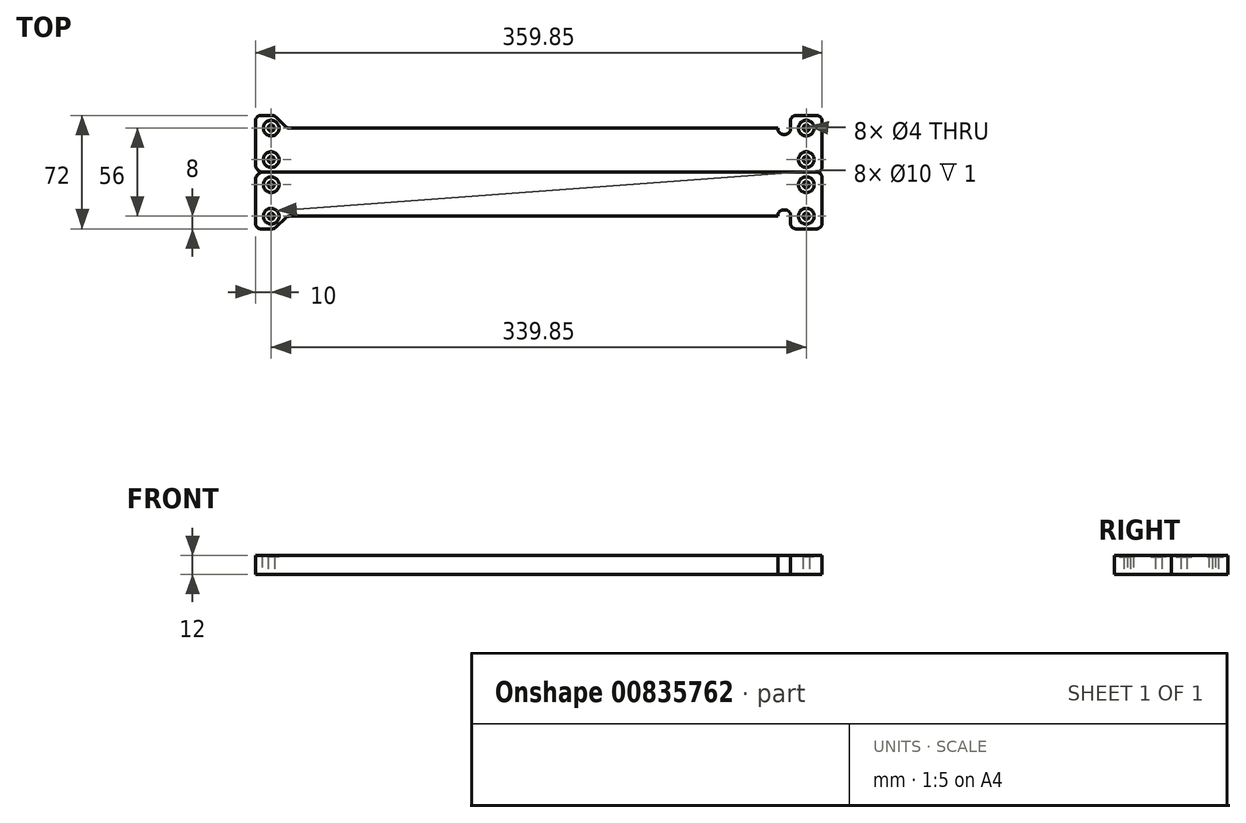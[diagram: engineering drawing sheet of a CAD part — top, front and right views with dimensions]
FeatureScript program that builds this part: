
annotation { "Feature Type Name" : "Feature", "Feature Type Description" : "" }
export const myFeature = defineFeature(function(context is Context, id is Id, definition is map)
    precondition{}
    {
        {
            var Q0;
            Q0=qCreatedBy(makeId("Top.planeOp"),FACE);
            var sketch = newSketch(context, id + "F0", { "sketchPlane" : qUnion([Q0])});
            skLineSegment(sketch, "E0", {"start": v(0, 0) * mm, "end": v(0, 28) * mm, "construction": true});
            skLineSegment(sketch, "E1", {"start": v(1.4, 28) * mm, "end": v(311.85, 28) * mm});
            skLineSegment(sketch, "E2", {"start": v(319.85, 28) * mm, "end": v(319.85, 32.6) * mm});
            skLineSegment(sketch, "E3", {"start": v(323.25, 36) * mm, "end": v(336.45, 36) * mm});
            skLineSegment(sketch, "E4", {"start": v(339.85, 32.6) * mm, "end": v(339.85, 3.4) * mm});
            skLineSegment(sketch, "E5", {"start": v(336.45, 0) * mm, "end": v(329.85, 0) * mm});
            skLineSegment(sketch, "E6", {"start": v(-1, 29) * mm, "end": v(-7, 35) * mm});
            skLineSegment(sketch, "E7", {"start": v(-9.4, 36) * mm, "end": v(-16.6, 36) * mm});
            skLineSegment(sketch, "E8", {"start": v(-20, 32.6) * mm, "end": v(-20, 4.95) * mm});
            skLineSegment(sketch, "E9", {"start": v(-10, 36) * mm, "end": v(-10, 0) * mm, "construction": true});
            skCircle(sketch, "E10", {"center": v(-10, 28) * mm, "radius": 2 * mm});
            skCircle(sketch, "E11", {"center": v(-10, 8) * mm, "radius": 2 * mm});
            skCircle(sketch, "E12", {"center": v(-10, 28) * mm, "radius": 5 * mm});
            skCircle(sketch, "E13", {"center": v(-10, 8) * mm, "radius": 5 * mm});
            skLineSegment(sketch, "E14", {"start": v(329.85, 36) * mm, "end": v(329.85, 0) * mm, "construction": true});
            skCircle(sketch, "E15", {"center": v(329.85, 8) * mm, "radius": 2 * mm});
            skCircle(sketch, "E16", {"center": v(329.85, 28) * mm, "radius": 2 * mm});
            skCircle(sketch, "E17", {"center": v(329.85, 28) * mm, "radius": 5 * mm});
            skCircle(sketch, "E18", {"center": v(329.85, 8) * mm, "radius": 5 * mm});
            skLineSegment(sketch, "E19", {"start": v(319.85, 28) * mm, "end": v(319.85, 27.4) * mm});
            skLineSegment(sketch, "E20", {"start": v(316.45, 24) * mm, "end": v(315.25, 24) * mm});
            skLineSegment(sketch, "E21", {"start": v(311.85, 27.4) * mm, "end": v(311.85, 28) * mm});
            skPoint(sketch, "E22.visualSharp", {"position": v(319.85, 36) * mm});
            skArc(sketch, "E22.filletArc", {"start": v(323.25, 36) * mm, "mid": v(320.85, 35) * mm, "end": v(319.85, 32.6) * mm});
            skPoint(sketch, "E23.visualSharp", {"position": v(319.85, 24) * mm});
            skArc(sketch, "E23.filletArc", {"start": v(316.45, 24) * mm, "mid": v(318.85, 25) * mm, "end": v(319.85, 27.4) * mm});
            skPoint(sketch, "E24.visualSharp", {"position": v(311.85, 24) * mm});
            skArc(sketch, "E24.filletArc", {"start": v(311.85, 27.4) * mm, "mid": v(312.85, 25) * mm, "end": v(315.25, 24) * mm});
            skPoint(sketch, "E25.visualSharp", {"position": v(339.85, 36) * mm});
            skArc(sketch, "E25.filletArc", {"start": v(339.85, 32.6) * mm, "mid": v(338.85, 35) * mm, "end": v(336.45, 36) * mm});
            skPoint(sketch, "E26.visualSharp", {"position": v(339.85, 0) * mm});
            skArc(sketch, "E26.filletArc", {"start": v(336.45, 0) * mm, "mid": v(338.85, 1) * mm, "end": v(339.85, 3.4) * mm});
            skPoint(sketch, "E27.visualSharp", {"position": v(-8, 36) * mm});
            skArc(sketch, "E27.filletArc", {"start": v(-7, 35) * mm, "mid": v(-8.1, 35.74) * mm, "end": v(-9.4, 36) * mm});
            skPoint(sketch, "E28.visualSharp", {"position": v(-20, 36) * mm});
            skArc(sketch, "E28.filletArc", {"start": v(-16.6, 36) * mm, "mid": v(-19, 35) * mm, "end": v(-20, 32.6) * mm});
            skPoint(sketch, "E29.visualSharp", {"position": v(-20, 0) * mm});
            skPoint(sketch, "E30.visualSharp", {"position": v(0, 28) * mm});
            skArc(sketch, "E30.filletArc", {"start": v(-1, 29) * mm, "mid": v(0.1, 28.26) * mm, "end": v(1.4, 28) * mm});
            skLineSegment(sketch, "E31", {"start": v(329.85, 0) * mm, "end": v(0, 0) * mm});
            skArc(sketch, "E32.filletArc", {"start": v(-20, 4.95) * mm, "mid": v(-18.78, 1.68) * mm, "end": v(-15.73, 0) * mm});
            skLineSegment(sketch, "E33", {"start": v(0, -16.1) * mm, "end": v(215.82, -16.1) * mm, "construction": true});
            skLineSegment(sketch, "E34", {"start": v(-15.73, 0) * mm, "end": v(0, 0) * mm});
            skSolve(sketch);
        }
        {
            var Q0;
            Q0=qSketchRegion(id+"F0",true);
            var Q1;
            Q1=makeQuery(id+"F0.imprint","IMPRINT",FACE,{"disambiguationData":[TD([[makeQuery(id+"F0.imprint","IMPRINT",EDGE,{"derivedFrom":sQuery(id+"F0.wireOp",EDGE,"E10")}),-1.0]])]});
            var Q2;
            Q2=makeQuery(id+"F0.imprint","IMPRINT",FACE,{"disambiguationData":[TD([[makeQuery(id+"F0.imprint","IMPRINT",EDGE,{"derivedFrom":sQuery(id+"F0.wireOp",EDGE,"E11")}),-1.0]])]});
            var Q3;
            Q3=makeQuery(id+"F0.imprint","IMPRINT",FACE,{"disambiguationData":[TD([[makeQuery(id+"F0.imprint","IMPRINT",EDGE,{"derivedFrom":sQuery(id+"F0.wireOp",EDGE,"E15")}),-1.0]])]});
            var Q4;
            Q4=makeQuery(id+"F0.imprint","IMPRINT",FACE,{"disambiguationData":[TD([[makeQuery(id+"F0.imprint","IMPRINT",EDGE,{"derivedFrom":sQuery(id+"F0.wireOp",EDGE,"E16")}),-1.0]])]});
            extrude(context, id + "F1", {"entities" : qUnion([Q0, Q1, Q2, Q3, Q4]), "depth" : 12 * mm, "offsetDistance" : 25 * mm});
        }
        {
            var Q0;
            Q0=makeQuery(id+"F1.opExtrude","CAP_FACE",FACE,{"disambiguationData":[OSD([sQuery(id+"F0.wireOp",EDGE,"E1"),sQuery(id+"F0.wireOp",EDGE,"E2"),sQuery(id+"F0.wireOp",EDGE,"E3"),sQuery(id+"F0.wireOp",EDGE,"E4"),sQuery(id+"F0.wireOp",EDGE,"E5"),sQuery(id+"F0.wireOp",EDGE,"E6"),sQuery(id+"F0.wireOp",EDGE,"E7"),sQuery(id+"F0.wireOp",EDGE,"E8"),sQuery(id+"F0.wireOp",EDGE,"QT8f5H8D-H1RM-RT4f-ZX45-cuhHGmmUbyoB"),sQuery(id+"F0.wireOp",EDGE,"E10"),sQuery(id+"F0.wireOp",EDGE,"E11"),sQuery(id+"F0.wireOp",EDGE,"E15"),sQuery(id+"F0.wireOp",EDGE,"E16"),sQuery(id+"F0.wireOp",EDGE,"E19"),sQuery(id+"F0.wireOp",EDGE,"E20"),sQuery(id+"F0.wireOp",EDGE,"E21"),sQuery(id+"F0.wireOp",EDGE,"E22.filletArc"),sQuery(id+"F0.wireOp",EDGE,"E23.filletArc"),sQuery(id+"F0.wireOp",EDGE,"E24.filletArc"),sQuery(id+"F0.wireOp",EDGE,"E25.filletArc"),sQuery(id+"F0.wireOp",EDGE,"E26.filletArc"),sQuery(id+"F0.wireOp",EDGE,"E27.filletArc"),sQuery(id+"F0.wireOp",EDGE,"E28.filletArc"),sQuery(id+"F0.wireOp",EDGE,"E29.filletArc"),sQuery(id+"F0.wireOp",EDGE,"E30.filletArc")])],"isStart":false});
            var sketch = newSketch(context, id + "F2", { "sketchPlane" : qUnion([Q0])});
            skCircle(sketch, "E35.0", {"center": v(329.85, 28) * mm, "radius": 5 * mm});
            skCircle(sketch, "E36.0", {"center": v(329.85, 8) * mm, "radius": 5 * mm});
            skCircle(sketch, "E37.0", {"center": v(-10, 8) * mm, "radius": 5 * mm});
            skCircle(sketch, "E38.0", {"center": v(-10, 28) * mm, "radius": 5 * mm});
            skSolve(sketch);
        }
        {
            var Q0;
            Q0=qSketchRegion(id+"F2",true);
            extrude(context, id + "F3", {"entities" : qUnion([Q0]), "operationType" : NewBodyOperationType.REMOVE, "oppositeDirection" : true, "depth" : 1 * mm, "offsetDistance" : 25 * mm});
        }
        {
            var Q0;
            Q0=makeQuery(id+"F1.opExtrude","CAP_FACE",FACE,{"disambiguationData":[OSD([sQuery(id+"F0.wireOp",EDGE,"E1"),sQuery(id+"F0.wireOp",EDGE,"E2"),sQuery(id+"F0.wireOp",EDGE,"E3"),sQuery(id+"F0.wireOp",EDGE,"E4"),sQuery(id+"F0.wireOp",EDGE,"E5"),sQuery(id+"F0.wireOp",EDGE,"E6"),sQuery(id+"F0.wireOp",EDGE,"E7"),sQuery(id+"F0.wireOp",EDGE,"E8"),sQuery(id+"F0.wireOp",EDGE,"QT8f5H8D-H1RM-RT4f-ZX45-cuhHGmmUbyoB"),sQuery(id+"F0.wireOp",EDGE,"E12"),sQuery(id+"F0.wireOp",EDGE,"E13"),sQuery(id+"F0.wireOp",EDGE,"E17"),sQuery(id+"F0.wireOp",EDGE,"E18"),sQuery(id+"F0.wireOp",EDGE,"E19"),sQuery(id+"F0.wireOp",EDGE,"E20"),sQuery(id+"F0.wireOp",EDGE,"E21"),sQuery(id+"F0.wireOp",EDGE,"E22.filletArc"),sQuery(id+"F0.wireOp",EDGE,"E23.filletArc"),sQuery(id+"F0.wireOp",EDGE,"E24.filletArc"),sQuery(id+"F0.wireOp",EDGE,"E25.filletArc"),sQuery(id+"F0.wireOp",EDGE,"E26.filletArc"),sQuery(id+"F0.wireOp",EDGE,"E27.filletArc"),sQuery(id+"F0.wireOp",EDGE,"E28.filletArc"),sQuery(id+"F0.wireOp",EDGE,"E29.filletArc"),sQuery(id+"F0.wireOp",EDGE,"E30.filletArc")])],"isStart":false});
            var sketch = newSketch(context, id + "F4", { "sketchPlane" : qUnion([Q0])});
            skLineSegment(sketch, "E39", {"start": v(6.93, 22.63) * mm, "end": v(6.93, 12.63) * mm});
            skArc(sketch, "E40.0.startCap", {"start": v(5.23, 22.63) * mm, "mid": v(6.93, 24.33) * mm, "end": v(8.63, 22.63) * mm});
            skArc(sketch, "E40.0.endCap", {"start": v(8.63, 12.63) * mm, "mid": v(6.93, 10.93) * mm, "end": v(5.23, 12.63) * mm});
            skLineSegment(sketch, "E40.0.left", {"start": v(8.63, 22.63) * mm, "end": v(8.63, 12.63) * mm});
            skLineSegment(sketch, "E40.0.right", {"start": v(5.23, 22.63) * mm, "end": v(5.23, 12.63) * mm});
            skArc(sketch, "E41.1.0.0", {"start": v(11.23, 22.63) * mm, "mid": v(12.93, 24.33) * mm, "end": v(14.63, 22.63) * mm});
            skLineSegment(sketch, "E41.1.0.1", {"start": v(11.23, 22.63) * mm, "end": v(11.23, 12.63) * mm});
            skLineSegment(sketch, "E41.1.0.2", {"start": v(14.63, 22.63) * mm, "end": v(14.63, 12.63) * mm});
            skArc(sketch, "E41.1.0.3", {"start": v(14.63, 12.63) * mm, "mid": v(12.93, 10.93) * mm, "end": v(11.23, 12.63) * mm});
            skLineSegment(sketch, "E41.direction1", {"start": v(5.23, 22.63) * mm, "end": v(11.23, 22.63) * mm, "construction": true});
            skSolve(sketch);
        }
        {
            var Q0;
            Q0=makeQuery(id+"F1.opExtrude","SWEPT_BODY",BODY,{"disambiguationData":[OSD([sQuery(id+"F0.wireOp",EDGE,"E1"),sQuery(id+"F0.wireOp",EDGE,"E2"),sQuery(id+"F0.wireOp",EDGE,"E3"),sQuery(id+"F0.wireOp",EDGE,"E4"),sQuery(id+"F0.wireOp",EDGE,"E5"),sQuery(id+"F0.wireOp",EDGE,"E6"),sQuery(id+"F0.wireOp",EDGE,"E7"),sQuery(id+"F0.wireOp",EDGE,"E8"),sQuery(id+"F0.wireOp",EDGE,"E10"),sQuery(id+"F0.wireOp",EDGE,"E11"),sQuery(id+"F0.wireOp",EDGE,"E15"),sQuery(id+"F0.wireOp",EDGE,"E16"),sQuery(id+"F0.wireOp",EDGE,"E19"),sQuery(id+"F0.wireOp",EDGE,"E20"),sQuery(id+"F0.wireOp",EDGE,"E21"),sQuery(id+"F0.wireOp",EDGE,"E22.filletArc"),sQuery(id+"F0.wireOp",EDGE,"E23.filletArc"),sQuery(id+"F0.wireOp",EDGE,"E24.filletArc"),sQuery(id+"F0.wireOp",EDGE,"E25.filletArc"),sQuery(id+"F0.wireOp",EDGE,"E26.filletArc"),sQuery(id+"F0.wireOp",EDGE,"E27.filletArc"),sQuery(id+"F0.wireOp",EDGE,"E28.filletArc"),sQuery(id+"F0.wireOp",EDGE,"E30.filletArc"),sQuery(id+"F0.wireOp",EDGE,"be8dcd3a-d1c8-49eb-a2e1-593493788622"),sQuery(id+"F0.wireOp",EDGE,"E32.filletArc")])]});
            var Q1;
            Q1=qCreatedBy(makeId("Front.planeOp"),FACE);
            mirror(context, id + "F5", {"entities" : qUnion([Q0]), "mirrorPlane" : qUnion([Q1])});
        }
    });
